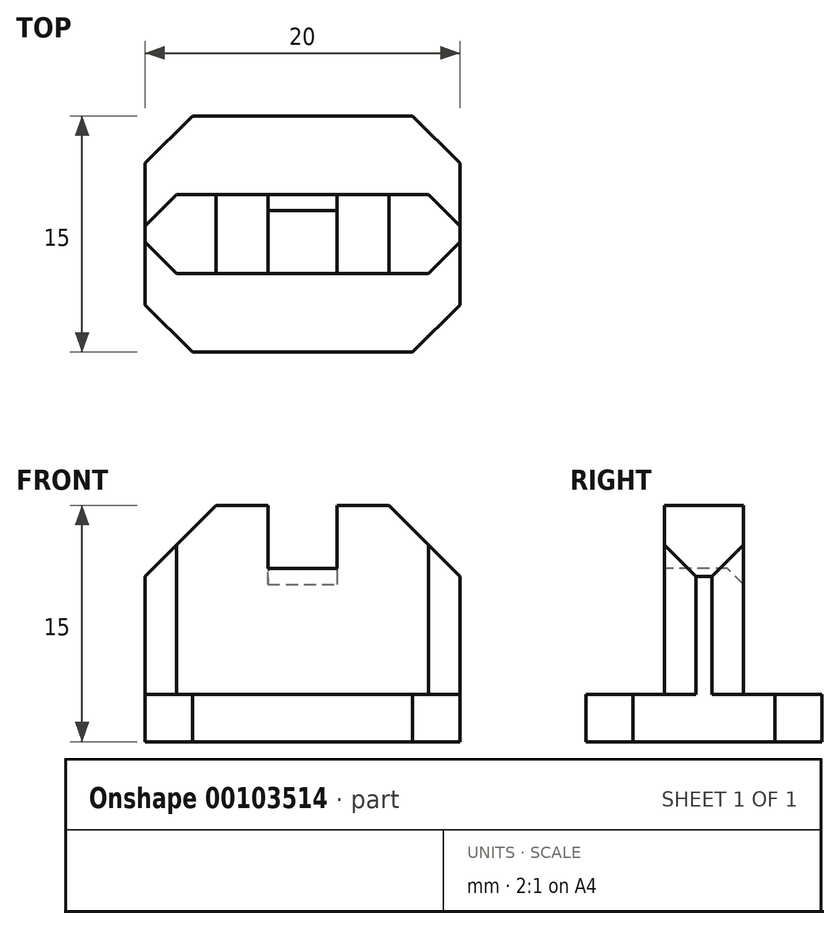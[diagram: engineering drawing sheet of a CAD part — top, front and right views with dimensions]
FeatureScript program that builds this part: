
annotation { "Feature Type Name" : "Feature", "Feature Type Description" : "" }
export const myFeature = defineFeature(function(context is Context, id is Id, definition is map)
    precondition{}
    {
        {
            var Q0;
            Q0=qCreatedBy(makeId("Top.planeOp"),FACE);
            var sketch = newSketch(context, id + "F0", { "sketchPlane" : qUnion([Q0])});
            skLineSegment(sketch, "E0.bottom", {"start": v(0, 0) * mm, "end": v(20, 0) * mm});
            skLineSegment(sketch, "E0.top", {"start": v(0, 15) * mm, "end": v(20, 15) * mm});
            skLineSegment(sketch, "E0.left", {"start": v(0, 0) * mm, "end": v(0, 15) * mm});
            skLineSegment(sketch, "E0.right", {"start": v(20, 0) * mm, "end": v(20, 15) * mm});
            skLineSegment(sketch, "E1", {"start": v(0, 10) * mm, "end": v(20, 10) * mm});
            skLineSegment(sketch, "E2", {"start": v(0, 5) * mm, "end": v(20, 5) * mm});
            skLineSegment(sketch, "E3", {"start": v(7.8, 10) * mm, "end": v(7.8, 5) * mm});
            skLineSegment(sketch, "E4", {"start": v(7.8, 5) * mm, "end": v(12.2, 5) * mm});
            skLineSegment(sketch, "E5", {"start": v(12.2, 5) * mm, "end": v(12.2, 10) * mm});
            skSolve(sketch);
        }
        {
            var Q0;
            {var subQ0=sQuery(id+"F0.wireOp",EDGE,"E0.top");Q0=makeQuery(id+"F0.imprint","IMPRINT",FACE,{"disambiguationData":[TD([[makeQuery(id+"F0.imprint","IMPRINT",EDGE,{"derivedFrom":subQ0}),-1.0]])]});}
            var Q1;
            {var subQ0=sQuery(id+"F0.wireOp",EDGE,"E1");Q1=makeQuery(id+"F0.imprint","IMPRINT",FACE,{"disambiguationData":[TD([[makeQuery(id+"F0.imprint","IMPRINT",EDGE,{"derivedFrom":subQ0}),-1.0]])]});}
            var Q2;
            {var subQ0=sQuery(id+"F0.wireOp",EDGE,"E0.bottom");Q2=makeQuery(id+"F0.imprint","IMPRINT",FACE,{"disambiguationData":[TD([[makeQuery(id+"F0.imprint","IMPRINT",EDGE,{"derivedFrom":subQ0}),1.0]])]});}
            extrude(context, id + "F1", {"entities" : qUnion([Q0, Q1, Q2]), "oppositeDirection" : true, "depth" : 3 * mm});
        }
        {
            var Q0;
            {var subQ5=sQuery(id+"F0.wireOp",EDGE,"E3");Q0=makeQuery(id+"F0.imprint","IMPRINT",FACE,{"disambiguationData":[TD([[makeQuery(id+"F0.imprint","IMPRINT",EDGE,{"derivedFrom":subQ5}),-1.0]])]});}
            var Q1;
            {var subQ5=sQuery(id+"F0.wireOp",EDGE,"E5");Q1=makeQuery(id+"F0.imprint","IMPRINT",FACE,{"disambiguationData":[TD([[makeQuery(id+"F0.imprint","IMPRINT",EDGE,{"derivedFrom":subQ5}),-1.0]])]});}
            extrude(context, id + "F2", {"entities" : qUnion([Q0, Q1]), "operationType" : NewBodyOperationType.ADD, "depth" : 12 * mm});
        }
        {
            var Q0;
            {var subQ0=sQuery(id+"F0.wireOp",EDGE,"E3");Q0=makeQuery(id+"F0.imprint","IMPRINT",FACE,{"disambiguationData":[TD([[makeQuery(id+"F0.imprint","IMPRINT",EDGE,{"derivedFrom":subQ0}),1.0]])]});}
            extrude(context, id + "F3", {"entities" : qUnion([Q0]), "operationType" : NewBodyOperationType.ADD, "depth" : 8 * mm});
        }
        {
            var Q0;
            Q0=makeQuery(id+"F2.opExtrude","SWEPT_EDGE",EDGE,{"disambiguationData":[OSD([sQuery(id+"F0.wireOp",EDGE,"E0.left"),sQuery(id+"F0.wireOp",EDGE,"E1")])]});
            var Q1;
            Q1=makeQuery(id+"F2.opExtrude","SWEPT_EDGE",EDGE,{"disambiguationData":[OSD([sQuery(id+"F0.wireOp",EDGE,"E0.left"),sQuery(id+"F0.wireOp",EDGE,"E2")])]});
            var Q2;
            Q2=makeQuery(id+"F2.opExtrude","SWEPT_EDGE",EDGE,{"disambiguationData":[OSD([sQuery(id+"F0.wireOp",EDGE,"E0.right"),sQuery(id+"F0.wireOp",EDGE,"E2")])]});
            var Q3;
            Q3=makeQuery(id+"F2.opExtrude","SWEPT_EDGE",EDGE,{"disambiguationData":[OSD([sQuery(id+"F0.wireOp",EDGE,"E0.right"),sQuery(id+"F0.wireOp",EDGE,"E1")])]});
            chamfer(context, id + "F4", {"entities" : qUnion([Q0, Q1, Q2, Q3]), "width" : 2 * mm, "tangentPropagation" : true});
        }
        {
            var Q0;
            Q0=makeQuery(id+"F2.opExtrude","CAP_EDGE",EDGE,{"disambiguationData":[OSD([sQuery(id+"F0.wireOp",EDGE,"E0.left")])],"isStart":false});
            var Q1;
            Q1=makeQuery(id+"F2.opExtrude","CAP_EDGE",EDGE,{"disambiguationData":[OSD([sQuery(id+"F0.wireOp",EDGE,"E0.right")])],"isStart":false});
            chamfer(context, id + "F5", {"entities" : qUnion([Q0, Q1]), "width" : 4.5 * mm, "tangentPropagation" : true});
        }
        {
            var Q0;
            Q0=makeQuery(id+"F1.opExtrude","SWEPT_EDGE",EDGE,{"disambiguationData":[OSD([sQuery(id+"F0.wireOp",EDGE,"E0.top"),sQuery(id+"F0.wireOp",EDGE,"E0.left")])]});
            var Q1;
            Q1=makeQuery(id+"F1.opExtrude","SWEPT_EDGE",EDGE,{"disambiguationData":[OSD([sQuery(id+"F0.wireOp",EDGE,"E0.bottom"),sQuery(id+"F0.wireOp",EDGE,"E0.left")])]});
            var Q2;
            Q2=makeQuery(id+"F1.opExtrude","SWEPT_EDGE",EDGE,{"disambiguationData":[OSD([sQuery(id+"F0.wireOp",EDGE,"E0.bottom"),sQuery(id+"F0.wireOp",EDGE,"E0.right")])]});
            var Q3;
            Q3=makeQuery(id+"F1.opExtrude","SWEPT_EDGE",EDGE,{"disambiguationData":[OSD([sQuery(id+"F0.wireOp",EDGE,"E0.top"),sQuery(id+"F0.wireOp",EDGE,"E0.right")])]});
            chamfer(context, id + "F6", {"entities" : qUnion([Q0, Q1, Q2, Q3]), "width" : 3 * mm, "tangentPropagation" : true});
        }
        {
            var Q0;
            Q0=makeQuery(id+"F3.opExtrude","CAP_EDGE",EDGE,{"disambiguationData":[OSD([sQuery(id+"F0.wireOp",EDGE,"E4")])],"isStart":false});
            var Q1;
            Q1=makeQuery(id+"F3.opExtrude","CAP_EDGE",EDGE,{"disambiguationData":[OSD([sQuery(id+"F0.wireOp",EDGE,"E1")])],"isStart":false});
            chamfer(context, id + "F7", {"entities" : qUnion([Q0, Q1]), "width" : 1 * mm, "tangentPropagation" : true});
        }
    });
